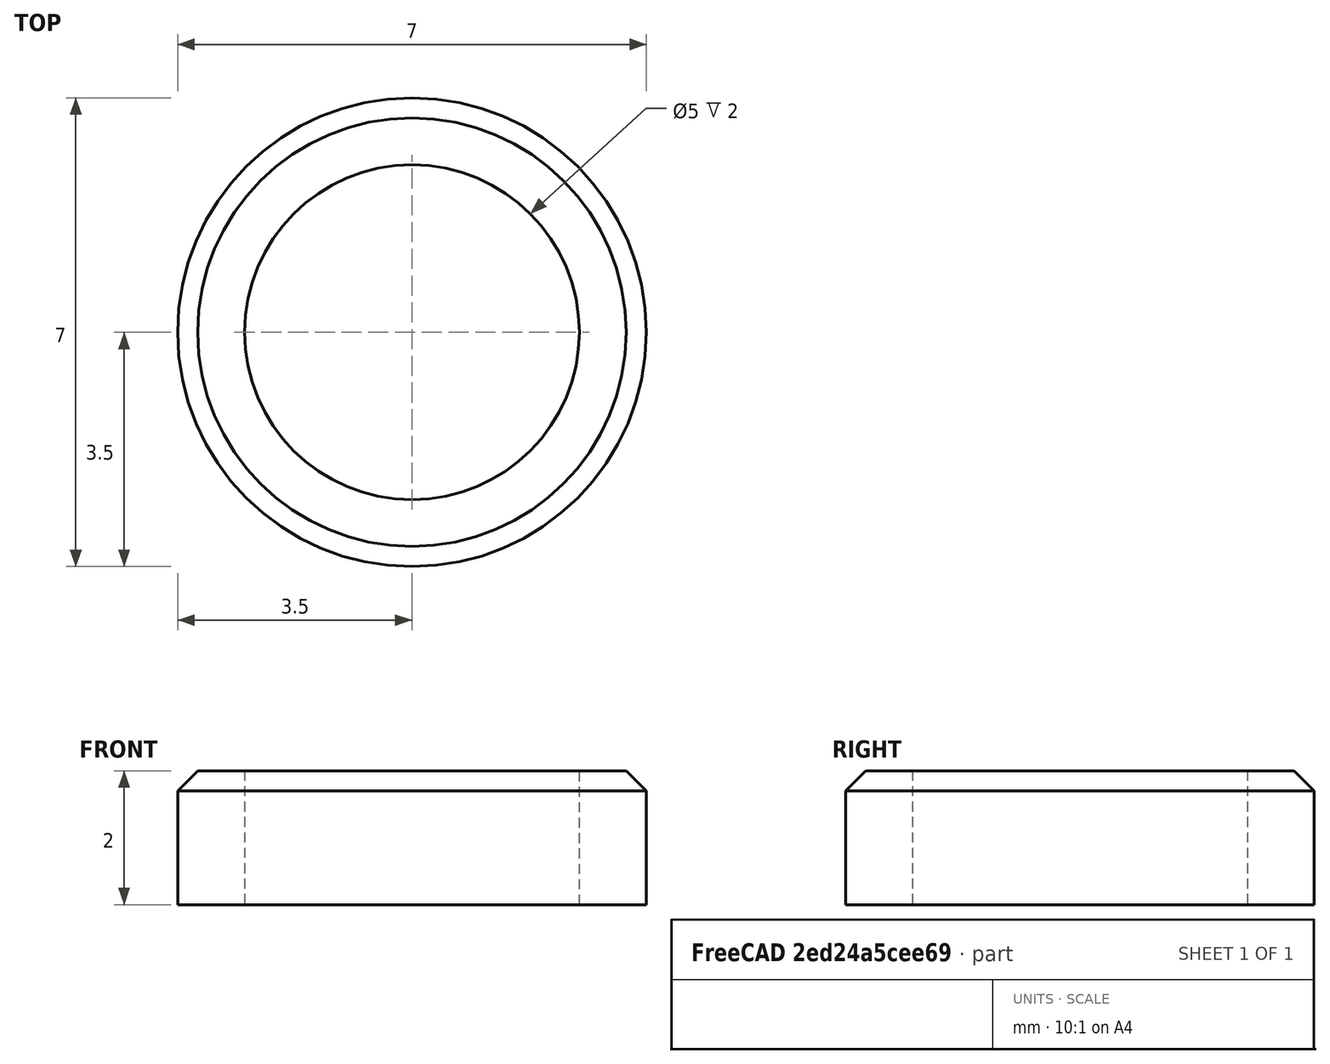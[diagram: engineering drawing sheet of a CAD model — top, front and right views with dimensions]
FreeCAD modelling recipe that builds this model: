
FCSTD DOCUMENT  (FreeCAD 0.19R24267 +99 (Git))
Label: buttonRing
License: All rights reserved
LicenseURL: http://en.wikipedia.org/wiki/All_rights_reserved
objects: Sketcher::SketchObject×1, PartDesign::Pad×1, PartDesign::Chamfer×1, PartDesign::Body×1
note: 6 computed .brp shape members not serialized (recipe doc carries the construction recipe); baked Part::Feature solids carry a one-line shape summary decoded from their .brp

FEATURE [Sketcher::SketchObject] Sketch
  FullyConstrained = true
  MapMode = 5
  Support = -> [XY_Plane]
  sketch-geometry (2):
    g0: Circle CenterX=0 CenterY=0 CenterZ=0 NormalX=0 NormalY=0 NormalZ=1 AngleXU=0 Radius=2.5
    g1: Circle CenterX=0 CenterY=0 CenterZ=0 NormalX=0 NormalY=0 NormalZ=1 AngleXU=0 Radius=3.5
  constraints (4):
    c: Coincident(g0,g-1)
    c: Coincident(g1,g0)
    c: Radius(g1) = 3.5
    c: Radius(g0) = 2.5
FEATURE [PartDesign::Pad] Pad
  Direction = (1,1,1)
  Length = 2
  Length2 = 100
  Profile = -> Sketch
  Type = 0
FEATURE [PartDesign::Chamfer] Chamfer
  Angle = 45
  Base = -> Pad [Edge3]
  BaseFeature = -> Pad
  ChamferType = 0
  FlipDirection = false
  Size = 0.3
  Size2 = 1
  SupportTransform = false
FEATURE [PartDesign::Body] Body
  Group = -> [Sketch,Pad,Chamfer]
  Origin = -> Origin
  Tip = -> Chamfer
